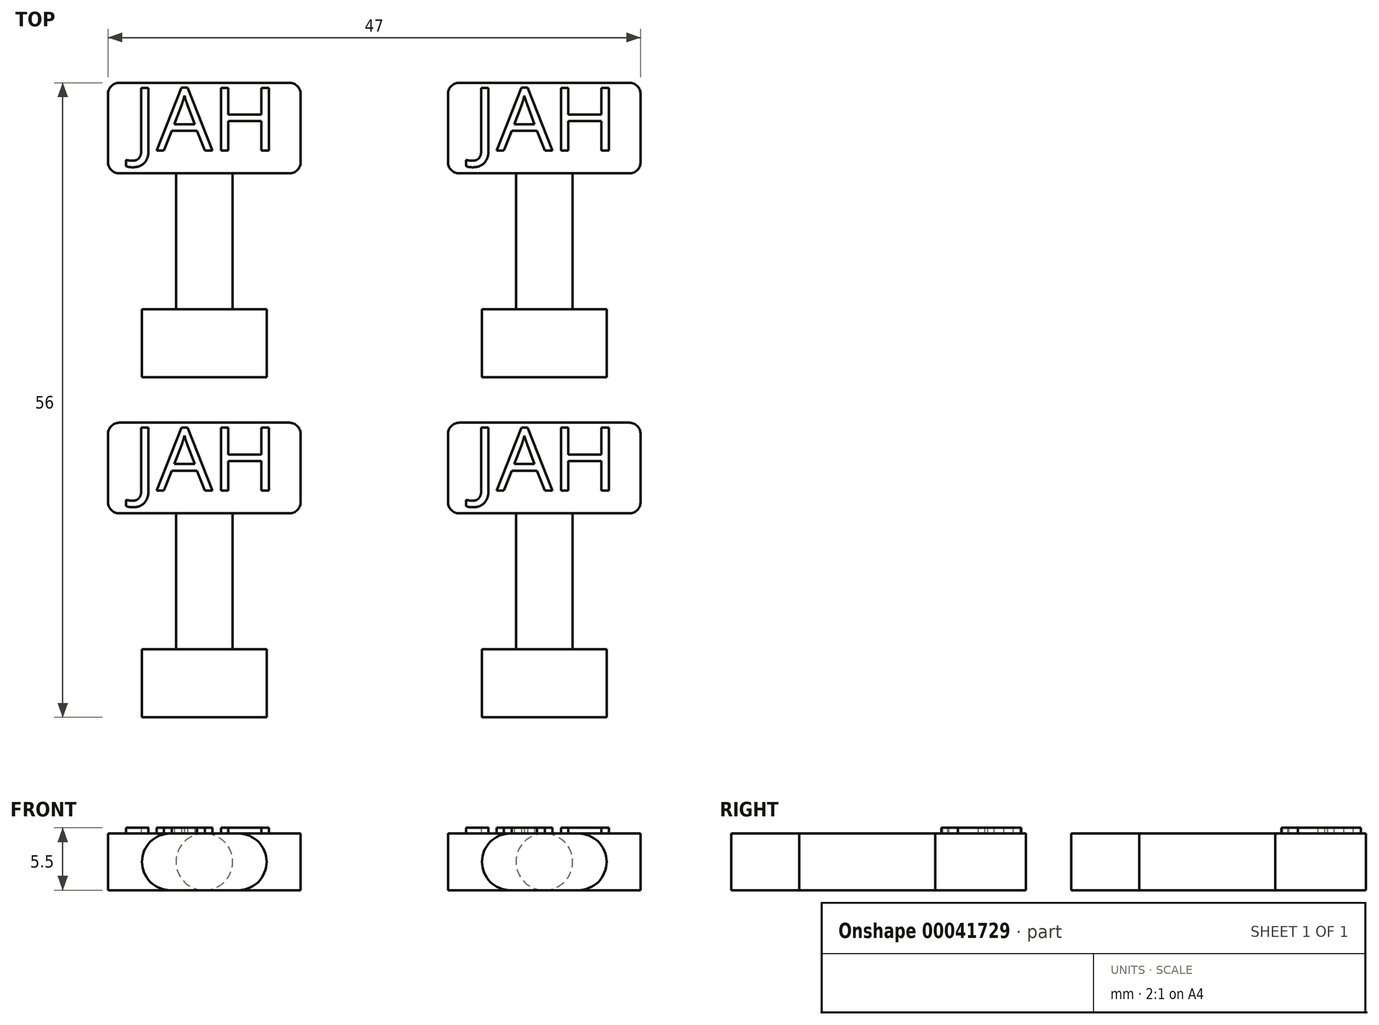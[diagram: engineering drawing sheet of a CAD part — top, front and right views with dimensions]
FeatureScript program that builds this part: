
annotation { "Feature Type Name" : "Feature", "Feature Type Description" : "" }
export const myFeature = defineFeature(function(context is Context, id is Id, definition is map)
    precondition{}
    {
        {
            var Q0;
            Q0=qCreatedBy(makeId("Top.planeOp"),FACE);
            var sketch = newSketch(context, id + "F0", { "sketchPlane" : qUnion([Q0])});
            skLineSegment(sketch, "E0", {"start": v(-12.5, 0) * mm, "end": v(12.5, 0) * mm, "construction": true});
            skLineSegment(sketch, "E1", {"start": v(12.5, 8.5) * mm, "end": v(12.5, -8.5) * mm, "construction": true});
            skLineSegment(sketch, "E2", {"start": v(12.5, 8.5) * mm, "end": v(4.5, 8.5) * mm});
            skLineSegment(sketch, "E3", {"start": v(4.5, 8.5) * mm, "end": v(4.5, -8.5) * mm});
            skLineSegment(sketch, "E4", {"start": v(4.5, -8.5) * mm, "end": v(12.5, -8.5) * mm});
            skLineSegment(sketch, "E5", {"start": v(12.5, 8.5) * mm, "end": v(12.5, -8.5) * mm});
            skSolve(sketch);
        }
        {
            var Q0;
            Q0=qSketchRegion(id+"F0",true);
            extrude(context, id + "F1", {"entities" : qUnion([Q0]), "depth" : 5 * mm});
        }
        {
            var Q0;
            Q0=makeQuery(id+"F1.opExtrude","SWEPT_FACE",FACE,{"disambiguationData":[OSD([sQuery(id+"F0.wireOp",EDGE,"E3")])]});
            var sketch = newSketch(context, id + "F2", { "sketchPlane" : qUnion([Q0])});
            skCircle(sketch, "E6", {"center": v(0, 2.5) * mm, "radius": 2.5 * mm});
            skPoint(sketch, "E6.first.point", {"position": v(0, 0) * mm});
            skPoint(sketch, "E6.second.point", {"position": v(0, 5) * mm});
            skPoint(sketch, "E6.third.point", {"position": v(2.35, 3.35) * mm});
            skSolve(sketch);
        }
        {
            var Q0;
            Q0=qSketchRegion(id+"F2",true);
            extrude(context, id + "F3", {"entities" : qUnion([Q0]), "operationType" : NewBodyOperationType.ADD, "depth" : 12 * mm});
        }
        {
            var Q0;
            Q0=makeQuery(id+"F3.opExtrude","CAP_FACE",FACE,{"disambiguationData":[OSD([sQuery(id+"F2.wireOp",EDGE,"E6")])],"isStart":false});
            var sketch = newSketch(context, id + "F4", { "sketchPlane" : qUnion([Q0])});
            skLineSegment(sketch, "E7", {"start": v(-5.5, 2.5) * mm, "end": v(5.5, 2.5) * mm, "construction": true});
            skPoint(sketch, "E8", {"position": v(0, 2.5) * mm});
            skCircle(sketch, "E9", {"center": v(-3, 2.5) * mm, "radius": 2.5 * mm});
            skLineSegment(sketch, "E10", {"start": v(0, 2.5) * mm, "end": v(0, 0) * mm, "construction": true});
            skCircle(sketch, "E11.MirrorC", {"center": v(3, 2.5) * mm, "radius": 2.5 * mm});
            skLineSegment(sketch, "E12", {"start": v(-3, 5) * mm, "end": v(3, 5) * mm});
            skLineSegment(sketch, "E13.MirrorCS", {"start": v(-3, 0) * mm, "end": v(3, 0) * mm});
            skSolve(sketch);
        }
        {
            var Q0;
            Q0=qSketchRegion(id+"F4",true);
            extrude(context, id + "F5", {"entities" : qUnion([Q0]), "operationType" : NewBodyOperationType.ADD, "depth" : 6 * mm});
        }
        {
            var Q0;
            Q0=makeQuery(id+"F1.opExtrude","SWEPT_BODY",BODY,{"disambiguationData":[OSD([sQuery(id+"F0.wireOp",EDGE,"E2"),sQuery(id+"F0.wireOp",EDGE,"E3"),sQuery(id+"F0.wireOp",EDGE,"E4"),sQuery(id+"F0.wireOp",EDGE,"E5")])]});
            var Q1;
            Q1=makeQuery(id+"F1.opExtrude","SWEPT_EDGE",EDGE,{"disambiguationData":[OSD([sQuery(id+"F0.wireOp",EDGE,"E4"),sQuery(id+"F0.wireOp",EDGE,"E5")])]});
            transform(context, id + "F6", {"entities" : qUnion([Q0]), "transformType" : TransformType.ROTATION, "transformAxis" : qUnion([Q1]), "angle" : 90 * degree, "oppositeDirection" : true, "makeCopy" : false});
        }
        {
            var Q0;
            Q0=makeQuery(id+"F1.opExtrude","CAP_FACE",FACE,{"disambiguationData":[OSD([sQuery(id+"F0.wireOp",EDGE,"E2"),sQuery(id+"F0.wireOp",EDGE,"E3"),sQuery(id+"F0.wireOp",EDGE,"E4"),sQuery(id+"F0.wireOp",EDGE,"E5")])],"isStart":false});
            var sketch = newSketch(context, id + "F7", { "sketchPlane" : qUnion([Q0])});
            skText(sketch, "E14", { "text": "JAH", "fontName": "OpenSans-Regular.ttf"});
            skLineSegment(sketch, "E15", {"start": v(-4.5, -14.5) * mm, "end": v(12.5, -14.5) * mm, "construction": true});
            skLineSegment(sketch, "E16", {"start": v(-4.5, -14.5) * mm, "end": v(-4.5, -16.5) * mm, "construction": true});
            const initialGuessF7  = {"E14": [-0.00229, -0.0145, 1, 0, 0.0056]};
            skSetInitialGuess(sketch, initialGuessF7);
            skSolve(sketch);
        }
        {
            var Q0;
            Q0=qSketchRegion(id+"F7",true);
            extrude(context, id + "F8", {"entities" : qUnion([Q0]), "operationType" : NewBodyOperationType.ADD, "depth" : .5 * mm});
        }
        {
            var Q0;
            Q0=makeQuery(id+"F1.opExtrude","SWEPT_EDGE",EDGE,{"disambiguationData":[OSD([sQuery(id+"F0.wireOp",EDGE,"E2"),sQuery(id+"F0.wireOp",EDGE,"E5")])]});
            var Q1;
            Q1=makeQuery(id+"F1.opExtrude","SWEPT_EDGE",EDGE,{"disambiguationData":[OSD([sQuery(id+"F0.wireOp",EDGE,"E2"),sQuery(id+"F0.wireOp",EDGE,"E3")])]});
            var Q2;
            Q2=makeQuery(id+"F1.opExtrude","SWEPT_EDGE",EDGE,{"disambiguationData":[OSD([sQuery(id+"F0.wireOp",EDGE,"E4"),sQuery(id+"F0.wireOp",EDGE,"E5")])]});
            var Q3;
            Q3=makeQuery(id+"F1.opExtrude","SWEPT_EDGE",EDGE,{"disambiguationData":[OSD([sQuery(id+"F0.wireOp",EDGE,"E3"),sQuery(id+"F0.wireOp",EDGE,"E4")])]});
            fillet(context, id + "F9", {"entities" : qUnion([Q0, Q1, Q2, Q3]), "radius" : 1 * mm, "tangentPropagation" : true, "allowEdgeOverflow" : false});
        }
        {
            var Q0;
            Q0=makeQuery(id+"F1.opExtrude","SWEPT_BODY",BODY,{"disambiguationData":[OSD([sQuery(id+"F0.wireOp",EDGE,"E2"),sQuery(id+"F0.wireOp",EDGE,"E3"),sQuery(id+"F0.wireOp",EDGE,"E4"),sQuery(id+"F0.wireOp",EDGE,"E5")])]});
            transform(context, id + "F10", {"entities" : qUnion([Q0]), "transformType" : TransformType.TRANSLATION_3D, "dx" : 30 * mm, "dy" : 0 * mm, "dz" : 0 * mm, "makeCopy" : true});
        }
        {
            var Q0;
            Q0=makeQuery(id+"F1.opExtrude","SWEPT_BODY",BODY,{"disambiguationData":[OSD([sQuery(id+"F0.wireOp",EDGE,"E2"),sQuery(id+"F0.wireOp",EDGE,"E3"),sQuery(id+"F0.wireOp",EDGE,"E4"),sQuery(id+"F0.wireOp",EDGE,"E5")])]});
            transform(context, id + "F11", {"entities" : qUnion([Q0]), "transformType" : TransformType.TRANSLATION_3D, "dx" : 0 * mm, "dy" : 30 * mm, "dz" : 0 * mm, "makeCopy" : true});
        }
        {
            var Q0;
            Q0=makeQuery(id+"F1.opExtrude","SWEPT_BODY",BODY,{"disambiguationData":[OSD([sQuery(id+"F0.wireOp",EDGE,"E2"),sQuery(id+"F0.wireOp",EDGE,"E3"),sQuery(id+"F0.wireOp",EDGE,"E4"),sQuery(id+"F0.wireOp",EDGE,"E5")])]});
            transform(context, id + "F12", {"entities" : qUnion([Q0]), "transformType" : TransformType.TRANSLATION_3D, "dx" : 30 * mm, "dy" : 30 * mm, "dz" : 0 * mm, "makeCopy" : true});
        }
    });
